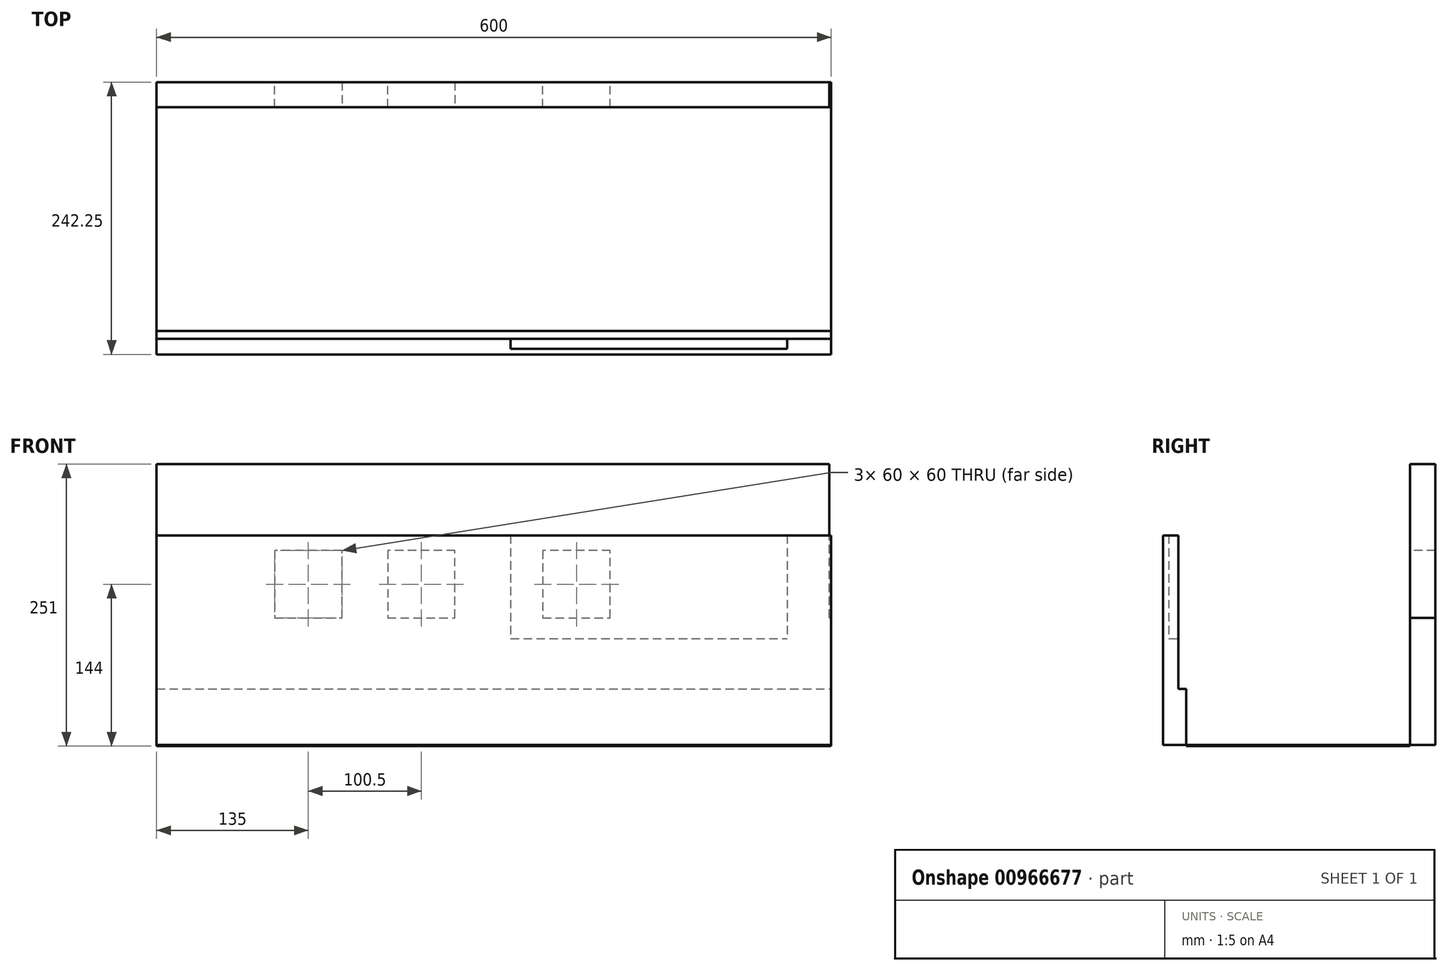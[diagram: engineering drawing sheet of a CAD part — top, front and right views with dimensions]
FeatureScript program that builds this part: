
annotation { "Feature Type Name" : "Feature", "Feature Type Description" : "" }
export const myFeature = defineFeature(function(context is Context, id is Id, definition is map)
    precondition{}
    {
        {
            var Q0;
            Q0=qCreatedBy(makeId("Top.planeOp"),FACE);
            var sketch = newSketch(context, id + "F0", { "sketchPlane" : qUnion([Q0])});
            skLineSegment(sketch, "E0.bottom", {"start": v(0, 0) * mm, "end": v(600, 0) * mm});
            skLineSegment(sketch, "E0.top", {"start": v(0, -199) * mm, "end": v(600, -199) * mm});
            skLineSegment(sketch, "E0.left", {"start": v(0, 0) * mm, "end": v(0, -199) * mm});
            skLineSegment(sketch, "E0.right", {"start": v(600, 0) * mm, "end": v(600, -199) * mm});
            skSolve(sketch);
        }
        {
            var Q0;
            Q0=makeQuery(id+"F0.imprint","IMPRINT",FACE,{"disambiguationData":[TD([[makeQuery(id+"F0.imprint","IMPRINT",EDGE,{"derivedFrom":sQuery(id+"F0.wireOp",EDGE,"E0.bottom")}),-1.0]])]});
            var sketch = newSketch(context, id + "F1", { "sketchPlane" : qUnion([Q0])});
            skLineSegment(sketch, "E1.bottom", {"start": v(0, 0) * mm, "end": v(600, 0) * mm});
            skLineSegment(sketch, "E1.top", {"start": v(0, 22.5) * mm, "end": v(600, 22.5) * mm});
            skLineSegment(sketch, "E1.left", {"start": v(0, 0) * mm, "end": v(0, 22.5) * mm});
            skLineSegment(sketch, "E1.right", {"start": v(600, 0) * mm, "end": v(600, 22.5) * mm});
            skSolve(sketch);
        }
        {
            var Q0;
            Q0=makeQuery(id+"F1.imprint","IMPRINT",FACE,{"disambiguationData":[TD([[makeQuery(id+"F1.imprint","IMPRINT",EDGE,{"derivedFrom":sQuery(id+"F1.wireOp",EDGE,"E1.bottom")}),1.0]])]});
            extrude(context, id + "F2", {"entities" : qUnion([Q0]), "depth" : 113 * mm, "offsetDistance" : 25 * mm});
        }
        {
            var Q0;
            Q0=makeQuery(id+"F2.opExtrude","CAP_FACE",FACE,{"disambiguationData":[OSD([sQuery(id+"F1.wireOp",EDGE,"E1.bottom"),sQuery(id+"F1.wireOp",EDGE,"E1.top"),sQuery(id+"F1.wireOp",EDGE,"E1.left"),sQuery(id+"F1.wireOp",EDGE,"E1.right")])],"isStart":false});
            var sketch = newSketch(context, id + "F3", { "sketchPlane" : qUnion([Q0])});
            skLineSegment(sketch, "E2.bottom", {"start": v(0, 0) * mm, "end": v(105, 0) * mm});
            skLineSegment(sketch, "E2.top", {"start": v(0, 22.5) * mm, "end": v(105, 22.5) * mm});
            skLineSegment(sketch, "E2.left", {"start": v(0, 0) * mm, "end": v(0, 22.5) * mm});
            skLineSegment(sketch, "E2.right", {"start": v(105, 0) * mm, "end": v(105, 22.5) * mm});
            skSolve(sketch);
        }
        {
            var Q0;
            Q0=makeQuery(id+"F3.imprint","IMPRINT",FACE,{"disambiguationData":[TD([[makeQuery(id+"F3.imprint","IMPRINT",EDGE,{"derivedFrom":sQuery(id+"F3.wireOp",EDGE,"E2.bottom")}),1.0]])]});
            extrude(context, id + "F4", {"entities" : qUnion([Q0]), "operationType" : NewBodyOperationType.ADD, "depth" : 137 * mm, "offsetDistance" : 25 * mm});
        }
        {
            var Q0;
            Q0=makeQuery(id+"F4.opExtrude","SWEPT_FACE",FACE,{"disambiguationData":[OSD([sQuery(id+"F3.wireOp",EDGE,"E2.right")])]});
            var sketch = newSketch(context, id + "F5", { "sketchPlane" : qUnion([Q0])});
            skLineSegment(sketch, "E3.bottom", {"start": v(0, 250) * mm, "end": v(22.5, 250) * mm});
            skLineSegment(sketch, "E3.top", {"start": v(0, 173) * mm, "end": v(22.5, 173) * mm});
            skLineSegment(sketch, "E3.left", {"start": v(0, 250) * mm, "end": v(0, 173) * mm});
            skLineSegment(sketch, "E3.right", {"start": v(22.5, 250) * mm, "end": v(22.5, 173) * mm});
            skSolve(sketch);
        }
        {
            var Q0;
            Q0=makeQuery(id+"F5.imprint","IMPRINT",FACE,{"disambiguationData":[TD([[makeQuery(id+"F5.imprint","IMPRINT",EDGE,{"derivedFrom":sQuery(id+"F5.wireOp",EDGE,"E3.bottom")}),-1.0]])]});
            extrude(context, id + "F6", {"entities" : qUnion([Q0]), "operationType" : NewBodyOperationType.ADD, "depth" : 100.5 * mm, "offsetDistance" : 25 * mm});
        }
        {
            var Q0;
            Q0=makeQuery(id+"F6.opExtrude","SWEPT_FACE",FACE,{"disambiguationData":[OSD([sQuery(id+"F5.wireOp",EDGE,"E3.top")])]});
            var sketch = newSketch(context, id + "F7", { "sketchPlane" : qUnion([Q0])});
            skLineSegment(sketch, "E4.bottom", {"start": v(205.5, -22.5) * mm, "end": v(165, -22.5) * mm});
            skLineSegment(sketch, "E4.top", {"start": v(205.5, 0) * mm, "end": v(165, 0) * mm});
            skLineSegment(sketch, "E4.left", {"start": v(205.5, -22.5) * mm, "end": v(205.5, 0) * mm});
            skLineSegment(sketch, "E4.right", {"start": v(165, -22.5) * mm, "end": v(165, 0) * mm});
            skSolve(sketch);
        }
        {
            var Q0;
            Q0=makeQuery(id+"F7.imprint","IMPRINT",FACE,{"disambiguationData":[TD([[makeQuery(id+"F7.imprint","IMPRINT",EDGE,{"derivedFrom":sQuery(id+"F7.wireOp",EDGE,"E4.bottom")}),-1.0]])]});
            extrude(context, id + "F8", {"entities" : qUnion([Q0]), "operationType" : NewBodyOperationType.ADD, "depth" : 61 * mm, "offsetDistance" : 25 * mm});
        }
        {
            var Q0;
            Q0=makeQuery(id+"F8.boolean.opBoolean","MERGE",FACE,{"derivedFrom":[makeQuery(id+"F6.opExtrude","CAP_FACE",FACE,{"disambiguationData":[OSD([sQuery(id+"F5.wireOp",EDGE,"E3.bottom"),sQuery(id+"F5.wireOp",EDGE,"E3.top"),sQuery(id+"F5.wireOp",EDGE,"E3.left"),sQuery(id+"F5.wireOp",EDGE,"E3.right")])],"isStart":false}),makeQuery(id+"F8.opExtrude","SWEPT_FACE",FACE,{"disambiguationData":[OSD([sQuery(id+"F7.wireOp",EDGE,"E4.left")])]})]});
            var sketch = newSketch(context, id + "F9", { "sketchPlane" : qUnion([Q0])});
            skLineSegment(sketch, "E5.bottom", {"start": v(0, 250) * mm, "end": v(22.5, 250) * mm});
            skLineSegment(sketch, "E5.top", {"start": v(0, 173) * mm, "end": v(22.5, 173) * mm});
            skLineSegment(sketch, "E5.left", {"start": v(0, 250) * mm, "end": v(0, 173) * mm});
            skLineSegment(sketch, "E5.right", {"start": v(22.5, 250) * mm, "end": v(22.5, 173) * mm});
            skSolve(sketch);
        }
        {
            var Q0;
            Q0=makeQuery(id+"F9.imprint","IMPRINT",FACE,{"disambiguationData":[TD([[makeQuery(id+"F9.imprint","IMPRINT",EDGE,{"derivedFrom":sQuery(id+"F9.wireOp",EDGE,"E5.bottom")}),-1.0]])]});
            extrude(context, id + "F10", {"entities" : qUnion([Q0]), "operationType" : NewBodyOperationType.ADD, "depth" : 138 * mm, "offsetDistance" : 25 * mm});
        }
        {
            var Q0;
            Q0=makeQuery(id+"F10.opExtrude","SWEPT_FACE",FACE,{"disambiguationData":[OSD([sQuery(id+"F9.wireOp",EDGE,"E5.top")])]});
            var sketch = newSketch(context, id + "F11", { "sketchPlane" : qUnion([Q0])});
            skLineSegment(sketch, "E6.bottom", {"start": v(343.5, -22.5) * mm, "end": v(265.5, -22.5) * mm});
            skLineSegment(sketch, "E6.top", {"start": v(343.5, 0) * mm, "end": v(265.5, 0) * mm});
            skLineSegment(sketch, "E6.left", {"start": v(343.5, -22.5) * mm, "end": v(343.5, 0) * mm});
            skLineSegment(sketch, "E6.right", {"start": v(265.5, -22.5) * mm, "end": v(265.5, 0) * mm});
            skSolve(sketch);
        }
        {
            var Q0;
            Q0=makeQuery(id+"F11.imprint","IMPRINT",FACE,{"disambiguationData":[TD([[makeQuery(id+"F11.imprint","IMPRINT",EDGE,{"derivedFrom":sQuery(id+"F11.wireOp",EDGE,"E6.bottom")}),-1.0]])]});
            extrude(context, id + "F12", {"entities" : qUnion([Q0]), "operationType" : NewBodyOperationType.ADD, "depth" : 61 * mm, "offsetDistance" : 25 * mm});
        }
        {
            var Q0;
            Q0=makeQuery(id+"F12.boolean.opBoolean","MERGE",FACE,{"derivedFrom":[makeQuery(id+"F10.opExtrude","CAP_FACE",FACE,{"disambiguationData":[OSD([sQuery(id+"F9.wireOp",EDGE,"E5.bottom"),sQuery(id+"F9.wireOp",EDGE,"E5.top"),sQuery(id+"F9.wireOp",EDGE,"E5.left"),sQuery(id+"F9.wireOp",EDGE,"E5.right")])],"isStart":false}),makeQuery(id+"F12.opExtrude","SWEPT_FACE",FACE,{"disambiguationData":[OSD([sQuery(id+"F11.wireOp",EDGE,"E6.left")])]})]});
            var sketch = newSketch(context, id + "F13", { "sketchPlane" : qUnion([Q0])});
            skLineSegment(sketch, "E7.bottom", {"start": v(22.5, 250) * mm, "end": v(0, 250) * mm});
            skLineSegment(sketch, "E7.top", {"start": v(22.5, 173) * mm, "end": v(0, 173) * mm});
            skLineSegment(sketch, "E7.left", {"start": v(22.5, 250) * mm, "end": v(22.5, 173) * mm});
            skLineSegment(sketch, "E7.right", {"start": v(0, 250) * mm, "end": v(0, 173) * mm});
            skSolve(sketch);
        }
        {
            var Q0;
            Q0=makeQuery(id+"F13.imprint","IMPRINT",FACE,{"disambiguationData":[TD([[makeQuery(id+"F13.imprint","IMPRINT",EDGE,{"derivedFrom":sQuery(id+"F13.wireOp",EDGE,"E7.bottom")}),-1.0]])]});
            extrude(context, id + "F14", {"entities" : qUnion([Q0]), "operationType" : NewBodyOperationType.ADD, "depth" : 60 * mm, "offsetDistance" : 25 * mm});
        }
        {
            var Q0;
            Q0=makeQuery(id+"F14.boolean.opBoolean","MERGE",FACE,{"derivedFrom":[makeQuery(id+"F10.boolean.opBoolean","MERGE",FACE,{"derivedFrom":[makeQuery(id+"F6.boolean.opBoolean","MERGE",FACE,{"derivedFrom":[makeQuery(id+"F4.opExtrude","CAP_FACE",FACE,{"disambiguationData":[OSD([sQuery(id+"F3.wireOp",EDGE,"E2.bottom"),sQuery(id+"F3.wireOp",EDGE,"E2.top"),sQuery(id+"F3.wireOp",EDGE,"E2.left"),sQuery(id+"F3.wireOp",EDGE,"E2.right")])],"isStart":false}),makeQuery(id+"F6.opExtrude","SWEPT_FACE",FACE,{"disambiguationData":[OSD([sQuery(id+"F5.wireOp",EDGE,"E3.bottom")])]})]}),makeQuery(id+"F10.opExtrude","SWEPT_FACE",FACE,{"disambiguationData":[OSD([sQuery(id+"F9.wireOp",EDGE,"E5.bottom")])]})]}),makeQuery(id+"F14.opExtrude","SWEPT_FACE",FACE,{"disambiguationData":[OSD([sQuery(id+"F13.wireOp",EDGE,"E7.bottom")])]})]});
            var sketch = newSketch(context, id + "F15", { "sketchPlane" : qUnion([Q0])});
            skLineSegment(sketch, "E8.bottom", {"start": v(403.5, 0) * mm, "end": v(598.5, 0) * mm});
            skLineSegment(sketch, "E8.top", {"start": v(403.5, 22.5) * mm, "end": v(598.5, 22.5) * mm});
            skLineSegment(sketch, "E8.left", {"start": v(403.5, 0) * mm, "end": v(403.5, 22.5) * mm});
            skLineSegment(sketch, "E8.right", {"start": v(598.5, 0) * mm, "end": v(598.5, 22.5) * mm});
            skSolve(sketch);
        }
        {
            var Q0;
            Q0=makeQuery(id+"F15.imprint","IMPRINT",FACE,{"disambiguationData":[TD([[makeQuery(id+"F15.imprint","IMPRINT",EDGE,{"derivedFrom":sQuery(id+"F15.wireOp",EDGE,"E8.bottom")}),1.0]])]});
            extrude(context, id + "F16", {"entities" : qUnion([Q0]), "operationType" : NewBodyOperationType.ADD, "oppositeDirection" : true, "depth" : 140 * mm, "offsetDistance" : 25 * mm});
        }
        {
            var Q0;
            Q0=makeQuery(id+"F0.imprint","IMPRINT",FACE,{"disambiguationData":[TD([[makeQuery(id+"F0.imprint","IMPRINT",EDGE,{"derivedFrom":sQuery(id+"F0.wireOp",EDGE,"E0.bottom")}),-1.0]])]});
            extrude(context, id + "F17", {"entities" : qUnion([Q0]), "oppositeDirection" : true, "depth" : 1 * mm, "offsetDistance" : 25 * mm});
        }
        {
            var Q0;
            Q0=makeQuery(id+"F17.opExtrude","CAP_FACE",FACE,{"disambiguationData":[OSD([sQuery(id+"F0.wireOp",EDGE,"E0.bottom"),sQuery(id+"F0.wireOp",EDGE,"E0.top"),sQuery(id+"F0.wireOp",EDGE,"E0.left"),sQuery(id+"F0.wireOp",EDGE,"E0.right")])],"isStart":true});
            var sketch = newSketch(context, id + "F18", { "sketchPlane" : qUnion([Q0])});
            skLineSegment(sketch, "E9.bottom", {"start": v(0, -199) * mm, "end": v(600, -199) * mm});
            skLineSegment(sketch, "E9.top", {"start": v(0, -228.5) * mm, "end": v(600, -228.5) * mm});
            skLineSegment(sketch, "E9.left", {"start": v(0, -199) * mm, "end": v(0, -228.5) * mm});
            skLineSegment(sketch, "E9.right", {"start": v(600, -199) * mm, "end": v(600, -228.5) * mm});
            skSolve(sketch);
        }
        {
            var Q0;
            Q0=makeQuery(id+"F18.imprint","IMPRINT",FACE,{"disambiguationData":[TD([[makeQuery(id+"F18.imprint","IMPRINT",EDGE,{"derivedFrom":sQuery(id+"F18.wireOp",EDGE,"E9.bottom")}),-1.0]])]});
            extrude(context, id + "F19", {"entities" : qUnion([Q0]), "depth" : 50 * mm, "offsetDistance" : 25 * mm});
        }
        {
            var Q0;
            Q0=makeQuery(id+"F19.opExtrude","CAP_FACE",FACE,{"disambiguationData":[OSD([sQuery(id+"F18.wireOp",EDGE,"E9.bottom"),sQuery(id+"F18.wireOp",EDGE,"E9.top"),sQuery(id+"F18.wireOp",EDGE,"E9.left"),sQuery(id+"F18.wireOp",EDGE,"E9.right")])],"isStart":false});
            var sketch = newSketch(context, id + "F20", { "sketchPlane" : qUnion([Q0])});
            skLineSegment(sketch, "E10.bottom", {"start": v(0, -228.5) * mm, "end": v(600, -228.5) * mm});
            skLineSegment(sketch, "E10.top", {"start": v(0, -206) * mm, "end": v(600, -206) * mm});
            skLineSegment(sketch, "E10.left", {"start": v(0, -228.5) * mm, "end": v(0, -206) * mm});
            skLineSegment(sketch, "E10.right", {"start": v(600, -228.5) * mm, "end": v(600, -206) * mm});
            skSolve(sketch);
        }
        {
            var Q0;
            Q0=makeQuery(id+"F20.imprint","IMPRINT",FACE,{"disambiguationData":[TD([[makeQuery(id+"F20.imprint","IMPRINT",EDGE,{"derivedFrom":sQuery(id+"F20.wireOp",EDGE,"E10.bottom")}),1.0]])]});
            extrude(context, id + "F21", {"entities" : qUnion([Q0]), "operationType" : NewBodyOperationType.ADD, "depth" : 136.5 * mm, "offsetDistance" : 25 * mm});
        }
        {
            var Q0;
            Q0=makeQuery(id+"F21.boolean.opBoolean","MERGE",FACE,{"derivedFrom":[makeQuery(id+"F19.opExtrude","SWEPT_FACE",FACE,{"disambiguationData":[OSD([sQuery(id+"F18.wireOp",EDGE,"E9.left")])]}),makeQuery(id+"F21.opExtrude","SWEPT_FACE",FACE,{"disambiguationData":[OSD([sQuery(id+"F20.wireOp",EDGE,"E10.left")])]})]});
            var sketch = newSketch(context, id + "F22", { "sketchPlane" : qUnion([Q0])});
            skLineSegment(sketch, "E11.bottom", {"start": v(228.5, 186.5) * mm, "end": v(206, 186.5) * mm});
            skLineSegment(sketch, "E11.top", {"start": v(228.5, 94.5) * mm, "end": v(206, 94.5) * mm});
            skLineSegment(sketch, "E11.left", {"start": v(228.5, 186.5) * mm, "end": v(228.5, 94.5) * mm});
            skLineSegment(sketch, "E11.right", {"start": v(206, 186.5) * mm, "end": v(206, 94.5) * mm});
            skSolve(sketch);
        }
        {
            var Q0;
            Q0=makeQuery(id+"F22.imprint","IMPRINT",FACE,{"disambiguationData":[TD([[makeQuery(id+"F22.imprint","IMPRINT",EDGE,{"derivedFrom":sQuery(id+"F22.wireOp",EDGE,"E11.bottom")}),-1.0]])]});
            extrude(context, id + "F23", {"entities" : qUnion([Q0]), "operationType" : NewBodyOperationType.REMOVE, "oppositeDirection" : true, "depth" : 561 * mm, "offsetDistance" : 25 * mm, "hasSecondDirection" : true, "secondDirectionOppositeDirection" : true, "secondDirectionDepth" : 315 * mm});
        }
        {
            var Q0;
            Q0=makeQuery(id+"F23.boolean.opBoolean","COPY",FACE,{"derivedFrom":makeQuery(id+"F23.opExtrude","SWEPT_FACE",FACE,{"disambiguationData":[OSD([sQuery(id+"F22.wireOp",EDGE,"E11.top")])]})});
            var sketch = newSketch(context, id + "F24", { "sketchPlane" : qUnion([Q0])});
            skLineSegment(sketch, "E12.bottom", {"start": v(315, -228.5) * mm, "end": v(630, -228.5) * mm});
            skLineSegment(sketch, "E12.top", {"start": v(315, -223.5) * mm, "end": v(630, -223.5) * mm});
            skLineSegment(sketch, "E12.left", {"start": v(315, -228.5) * mm, "end": v(315, -223.5) * mm});
            skLineSegment(sketch, "E12.right", {"start": v(630, -228.5) * mm, "end": v(630, -223.5) * mm});
            skSolve(sketch);
        }
        {
            var Q0;
            {var subQ0=sQuery(id+"F24.wireOp",EDGE,"E12.left");Q0=makeQuery(id+"F24.imprint","IMPRINT",FACE,{"disambiguationData":[TD([[makeQuery(id+"F24.imprint","IMPRINT",EDGE,{"derivedFrom":subQ0}),-1.0]])]});}
            extrude(context, id + "F25", {"entities" : qUnion([Q0]), "depth" : 92 * mm, "offsetDistance" : 25 * mm});
        }
        {
            var Q0;
            Q0=makeQuery(id+"F25.opExtrude","SWEPT_FACE",FACE,{"disambiguationData":[OSD([sQuery(id+"F24.wireOp",EDGE,"E12.top")])]});
            extrude(context, id + "F26", {"entities" : qUnion([Q0]), "operationType" : NewBodyOperationType.ADD, "depth" : 8.75 * mm, "offsetDistance" : 25 * mm});
        }
        {
            var Q0;
            Q0=makeQuery(id+"F25.opExtrude","SWEPT_FACE",FACE,{"disambiguationData":[OSD([sQuery(id+"F24.wireOp",EDGE,"E12.bottom")])]});
            extrude(context, id + "F27", {"entities" : qUnion([Q0]), "operationType" : NewBodyOperationType.REMOVE, "oppositeDirection" : true, "depth" : 8.75 * mm, "offsetDistance" : 25 * mm});
        }
    });
